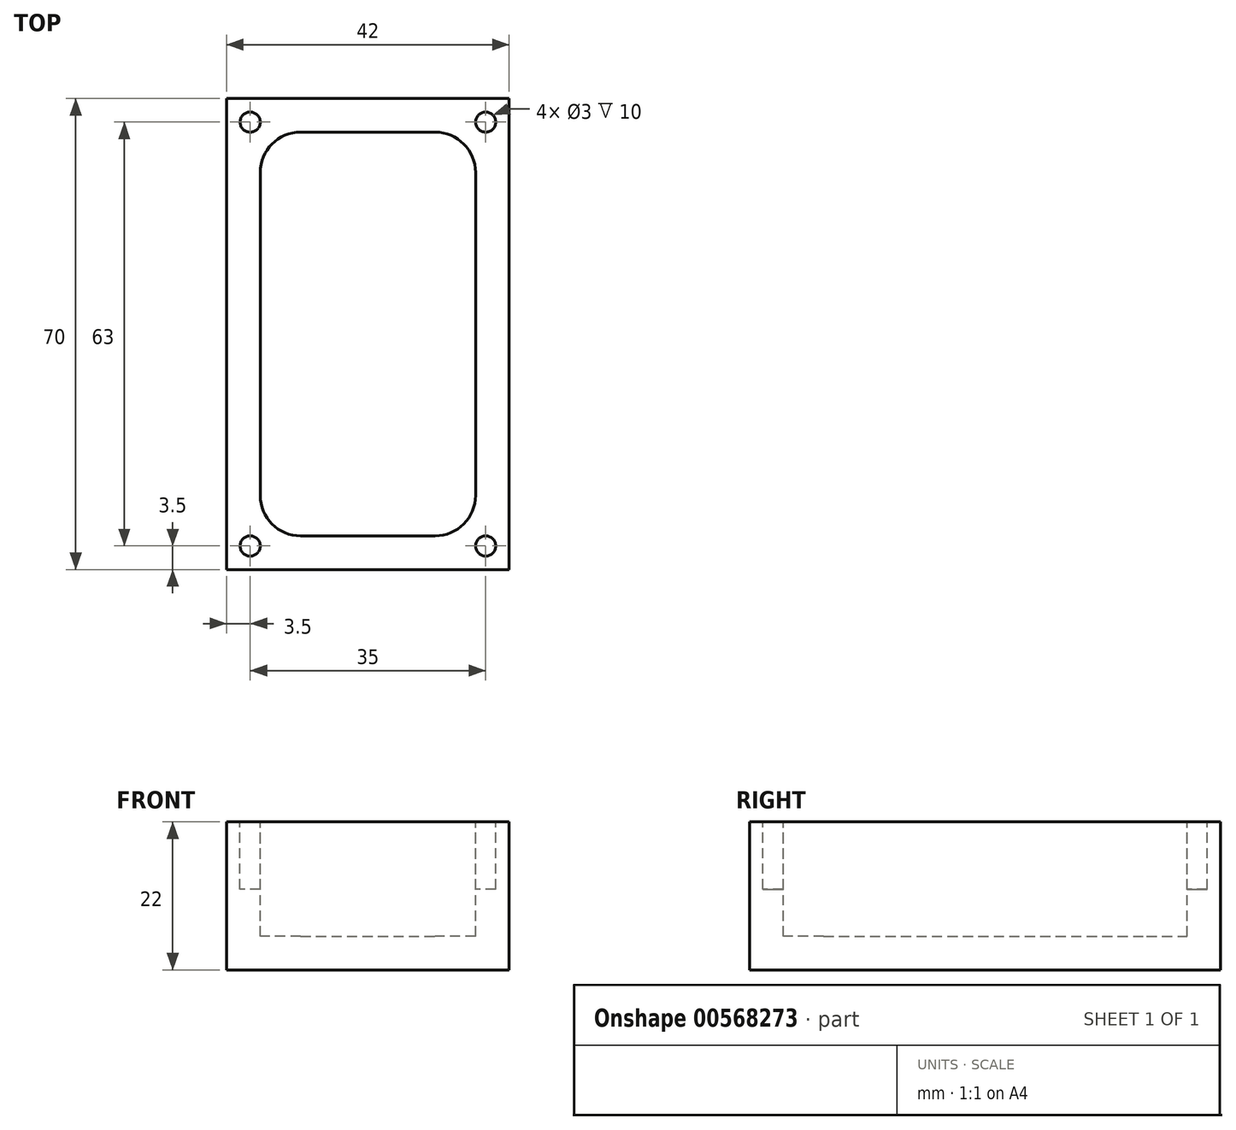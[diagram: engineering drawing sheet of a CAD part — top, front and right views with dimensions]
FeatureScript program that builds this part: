
annotation { "Feature Type Name" : "Feature", "Feature Type Description" : "" }
export const myFeature = defineFeature(function(context is Context, id is Id, definition is map)
    precondition{}
    {
        {
            var Q0;
            Q0=qCreatedBy(makeId("Top.planeOp"),FACE);
            var sketch = newSketch(context, id + "F0", { "sketchPlane" : qUnion([Q0])});
            skLineSegment(sketch, "E0.bottom", {"start": v(0, 0) * mm, "end": v(42, 0) * mm});
            skLineSegment(sketch, "E0.top", {"start": v(0, 70) * mm, "end": v(42, 70) * mm});
            skLineSegment(sketch, "E0.left", {"start": v(0, 0) * mm, "end": v(0, 70) * mm});
            skLineSegment(sketch, "E0.right", {"start": v(42, 0) * mm, "end": v(42, 70) * mm});
            skSolve(sketch);
        }
        {
            var Q0;
            Q0 = qSketchRegion(id + "F0", true);
            extrude(context, id + "F1", {"entities" : qUnion([Q0]), "depth" : 22 * mm, "offsetDistance" : 25 * mm});
        }
        {
            var Q0;
            Q0=makeQuery(id+"F1.opExtrude","CAP_FACE",FACE,{"disambiguationData":[OSD([sQuery(id+"F0.wireOp",EDGE,"E0.bottom"),sQuery(id+"F0.wireOp",EDGE,"E0.top"),sQuery(id+"F0.wireOp",EDGE,"E0.left"),sQuery(id+"F0.wireOp",EDGE,"E0.right")])],"isStart":false});
            var sketch = newSketch(context, id + "F2", { "sketchPlane" : qUnion([Q0])});
            skLineSegment(sketch, "E1.0", {"start": v(37, 11) * mm, "end": v(37, 59) * mm});
            skLineSegment(sketch, "E1.1", {"start": v(11, 5) * mm, "end": v(31, 5) * mm});
            skLineSegment(sketch, "E1.2", {"start": v(5, 11) * mm, "end": v(5, 59) * mm});
            skLineSegment(sketch, "E1.3", {"start": v(11, 65) * mm, "end": v(31, 65) * mm});
            skPoint(sketch, "E2.visualSharp", {"position": v(5, 65) * mm});
            skArc(sketch, "E2.filletArc", {"start": v(11, 65) * mm, "mid": v(6.76, 63.24) * mm, "end": v(5, 59) * mm});
            skPoint(sketch, "E3.visualSharp", {"position": v(37, 65) * mm});
            skArc(sketch, "E3.filletArc", {"start": v(37, 59) * mm, "mid": v(35.24, 63.24) * mm, "end": v(31, 65) * mm});
            skPoint(sketch, "E4.visualSharp", {"position": v(37, 5) * mm});
            skArc(sketch, "E4.filletArc", {"start": v(31, 5) * mm, "mid": v(35.24, 6.76) * mm, "end": v(37, 11) * mm});
            skPoint(sketch, "E5.visualSharp", {"position": v(5, 5) * mm});
            skArc(sketch, "E5.filletArc", {"start": v(5, 11) * mm, "mid": v(6.76, 6.76) * mm, "end": v(11, 5) * mm});
            skSolve(sketch);
        }
        {
            var Q0;
            Q0 = qSketchRegion(id + "F2", true);
            extrude(context, id + "F3", {"entities" : qUnion([Q0]), "operationType" : NewBodyOperationType.REMOVE, "oppositeDirection" : true, "depth" : (22 - 5) * mm, "offsetDistance" : 25 * mm});
        }
        {
            var Q0;
            Q0=makeQuery(id+"F1.opExtrude","CAP_FACE",FACE,{"disambiguationData":[OSD([sQuery(id+"F0.wireOp",EDGE,"E0.bottom"),sQuery(id+"F0.wireOp",EDGE,"E0.top"),sQuery(id+"F0.wireOp",EDGE,"E0.left"),sQuery(id+"F0.wireOp",EDGE,"E0.right")])],"isStart":false});
            var sketch = newSketch(context, id + "F4", { "sketchPlane" : qUnion([Q0])});
            skCircle(sketch, "E6", {"center": v(3.5, 66.5) * mm, "radius": 1.5 * mm});
            skCircle(sketch, "E7", {"center": v(38.5, 66.5) * mm, "radius": 1.5 * mm});
            skCircle(sketch, "E8", {"center": v(38.5, 3.5) * mm, "radius": 1.5 * mm});
            skCircle(sketch, "E9", {"center": v(3.5, 3.5) * mm, "radius": 1.5 * mm});
            skSolve(sketch);
        }
        {
            var Q0;
            Q0 = qSketchRegion(id + "F4", true);
            extrude(context, id + "F5", {"entities" : qUnion([Q0]), "operationType" : NewBodyOperationType.REMOVE, "oppositeDirection" : true, "depth" : 10 * mm, "offsetDistance" : 25 * mm});
        }
    });
